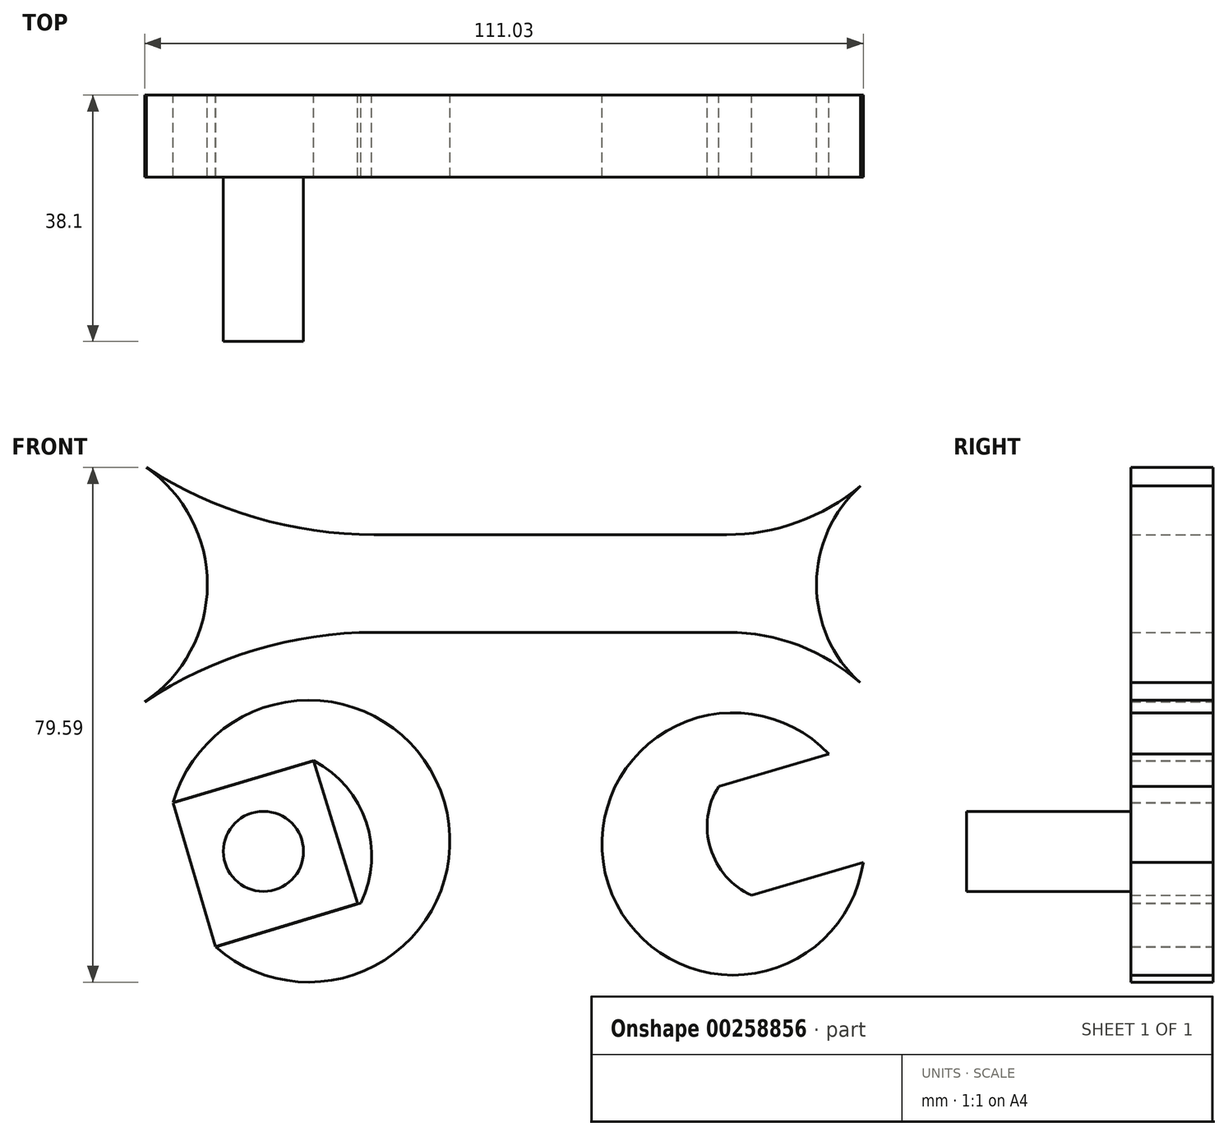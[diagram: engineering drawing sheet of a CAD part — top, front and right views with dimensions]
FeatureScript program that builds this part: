
annotation { "Feature Type Name" : "Feature", "Feature Type Description" : "" }
export const myFeature = defineFeature(function(context is Context, id is Id, definition is map)
    precondition{}
    {
        {
            var Q0;
            Q0=qCreatedBy(makeId("Front.planeOp"),FACE);
            var sketch = newSketch(context, id + "F0", { "sketchPlane" : qUnion([Q0])});
            skLineSegment(sketch, "E0", {"start": v(-20.53, 29.23) * mm, "end": v(33.9, 29.23) * mm});
            skLineSegment(sketch, "E1", {"start": v(34.18, 14.12) * mm, "end": v(-20.48, 14.12) * mm});
            skLineSegment(sketch, "E2", {"start": v(-45.01, -34.56) * mm, "end": v(-22.6, -27.75) * mm});
            skLineSegment(sketch, "E3", {"start": v(-51.59, -12.15) * mm, "end": v(-29.86, -5.72) * mm});
            skLineSegment(sketch, "E4", {"start": v(37.8, -26.54) * mm, "end": v(55.04, -21.44) * mm});
            skLineSegment(sketch, "E5", {"start": v(32.69, -9.7) * mm, "end": v(49.73, -4.7) * mm});
            skArc(sketch, "E6", {"start": v(-55.76, 39.62) * mm, "mid": v(-38.9, 31.88) * mm, "end": v(-20.53, 29.23) * mm});
            skArc(sketch, "E7", {"start": v(-20.48, 14.12) * mm, "mid": v(-39.03, 11.38) * mm, "end": v(-55.99, 3.39) * mm});
            skArc(sketch, "E8", {"start": v(-55.99, 3.39) * mm, "mid": v(-46.32, 21.44) * mm, "end": v(-55.76, 39.62) * mm});
            skArc(sketch, "E9", {"start": v(33.9, 29.23) * mm, "mid": v(44.94, 31.17) * mm, "end": v(54.65, 36.76) * mm});
            skArc(sketch, "E10", {"start": v(54.65, 36.76) * mm, "mid": v(47.81, 21.5) * mm, "end": v(54.65, 6.25) * mm});
            skArc(sketch, "E11", {"start": v(54.65, 6.25) * mm, "mid": v(45.14, 12.09) * mm, "end": v(34.18, 14.12) * mm});
            skArc(sketch, "E12", {"start": v(-45.01, -34.56) * mm, "mid": v(-9.72, -12.03) * mm, "end": v(-51.59, -12.15) * mm});
            skArc(sketch, "E13", {"start": v(49.73, -4.7) * mm, "mid": v(15.62, -24.73) * mm, "end": v(55.04, -21.44) * mm});
            skArc(sketch, "E14", {"start": v(32.69, -9.7) * mm, "mid": v(31.44, -19.28) * mm, "end": v(37.8, -26.54) * mm});
            skArc(sketch, "E15", {"start": v(-22.6, -27.75) * mm, "mid": v(-21.76, -15.26) * mm, "end": v(-29.86, -5.72) * mm});
            skLineSegment(sketch, "E16", {"start": v(-29.86, -5.72) * mm, "end": v(-51.59, -12.15) * mm});
            skLineSegment(sketch, "E17", {"start": v(-22.6, -27.75) * mm, "end": v(-29.86, -5.72) * mm});
            skLineSegment(sketch, "E18", {"start": v(-45.01, -34.56) * mm, "end": v(-51.82, -12.15) * mm});
            skSolve(sketch);
        }
        {
            var Q0;
            Q0=makeQuery(id+"F0.imprint","IMPRINT",FACE,{"disambiguationData":[TD([[makeQuery(id+"F0.imprint","IMPRINT",EDGE,{"derivedFrom":sQuery(id+"F0.wireOp",EDGE,"E2")}),-1.0]])]});
            var Q1;
            Q1=sQuery(id+"F0.wireOp",EDGE,"E12");
            var Q2;
            Q2=sQuery(id+"F0.wireOp",EDGE,"E2");
            var Q3;
            Q3=sQuery(id+"F0.wireOp",EDGE,"E3");
            var Q4;
            Q4=sQuery(id+"F0.wireOp",EDGE,"E15");
            extrude(context, id + "F1", {"entities" : qUnion([Q0]), "surfaceEntities" : qUnion([Q1, Q2, Q3, Q4]), "endBound" : BoundingType.SYMMETRIC, "depth" : 12.7 * mm});
        }
        {
            var Q0;
            Q0=makeQuery(id+"F0.imprint","IMPRINT",FACE,{"disambiguationData":[TD([[makeQuery(id+"F0.imprint","IMPRINT",EDGE,{"derivedFrom":sQuery(id+"F0.wireOp",EDGE,"E4")}),-1.0]])]});
            extrude(context, id + "F2", {"entities" : qUnion([Q0]), "endBound" : BoundingType.SYMMETRIC, "depth" : 12.7 * mm});
        }
        {
            var Q0;
            Q0=makeQuery(id+"F0.imprint","IMPRINT",FACE,{"disambiguationData":[TD([[makeQuery(id+"F0.imprint","IMPRINT",EDGE,{"derivedFrom":sQuery(id+"F0.wireOp",EDGE,"E0")}),-1.0]])]});
            extrude(context, id + "F3", {"entities" : qUnion([Q0]), "endBound" : BoundingType.SYMMETRIC, "depth" : 12.7 * mm});
        }
        {
            var Q0;
            Q0=qCreatedBy(makeId("Front.planeOp"),FACE);
            var sketch = newSketch(context, id + "F4", { "sketchPlane" : qUnion([Q0])});
            skLineSegment(sketch, "E19", {"start": v(-51.6, -12.22) * mm, "end": v(-29.87, -5.77) * mm});
            skLineSegment(sketch, "E20", {"start": v(-29.87, -5.77) * mm, "end": v(-23.1, -27.78) * mm});
            skLineSegment(sketch, "E21", {"start": v(-23.1, -27.78) * mm, "end": v(-45.04, -34.46) * mm});
            skLineSegment(sketch, "E22", {"start": v(-45.04, -34.46) * mm, "end": v(-51.6, -12.22) * mm});
            skSolve(sketch);
        }
        {
            var Q0;
            Q0 = qSketchRegion(id + "F4", true);
            extrude(context, id + "F5", {"entities" : qUnion([Q0]), "endBound" : BoundingType.SYMMETRIC, "depth" : 12.7 * mm});
        }
        {
            var Q0;
            Q0=makeQuery(id+"F5.opExtrude","CAP_FACE",FACE,{"disambiguationData":[OSD([sQuery(id+"F4.wireOp",EDGE,"E19"),sQuery(id+"F4.wireOp",EDGE,"E20"),sQuery(id+"F4.wireOp",EDGE,"E21"),sQuery(id+"F4.wireOp",EDGE,"E22")])],"isStart":false});
            var sketch = newSketch(context, id + "F6", { "sketchPlane" : qUnion([Q0])});
            skCircle(sketch, "E23", {"center": v(-37.65, -19.75) * mm, "radius": 6.2 * mm});
            skSolve(sketch);
        }
        {
            var Q0;
            Q0 = qSketchRegion(id + "F6", true);
            extrude(context, id + "F7", {"entities" : qUnion([Q0]), "operationType" : NewBodyOperationType.ADD, "depth" : 25.4 * mm});
        }
    });
